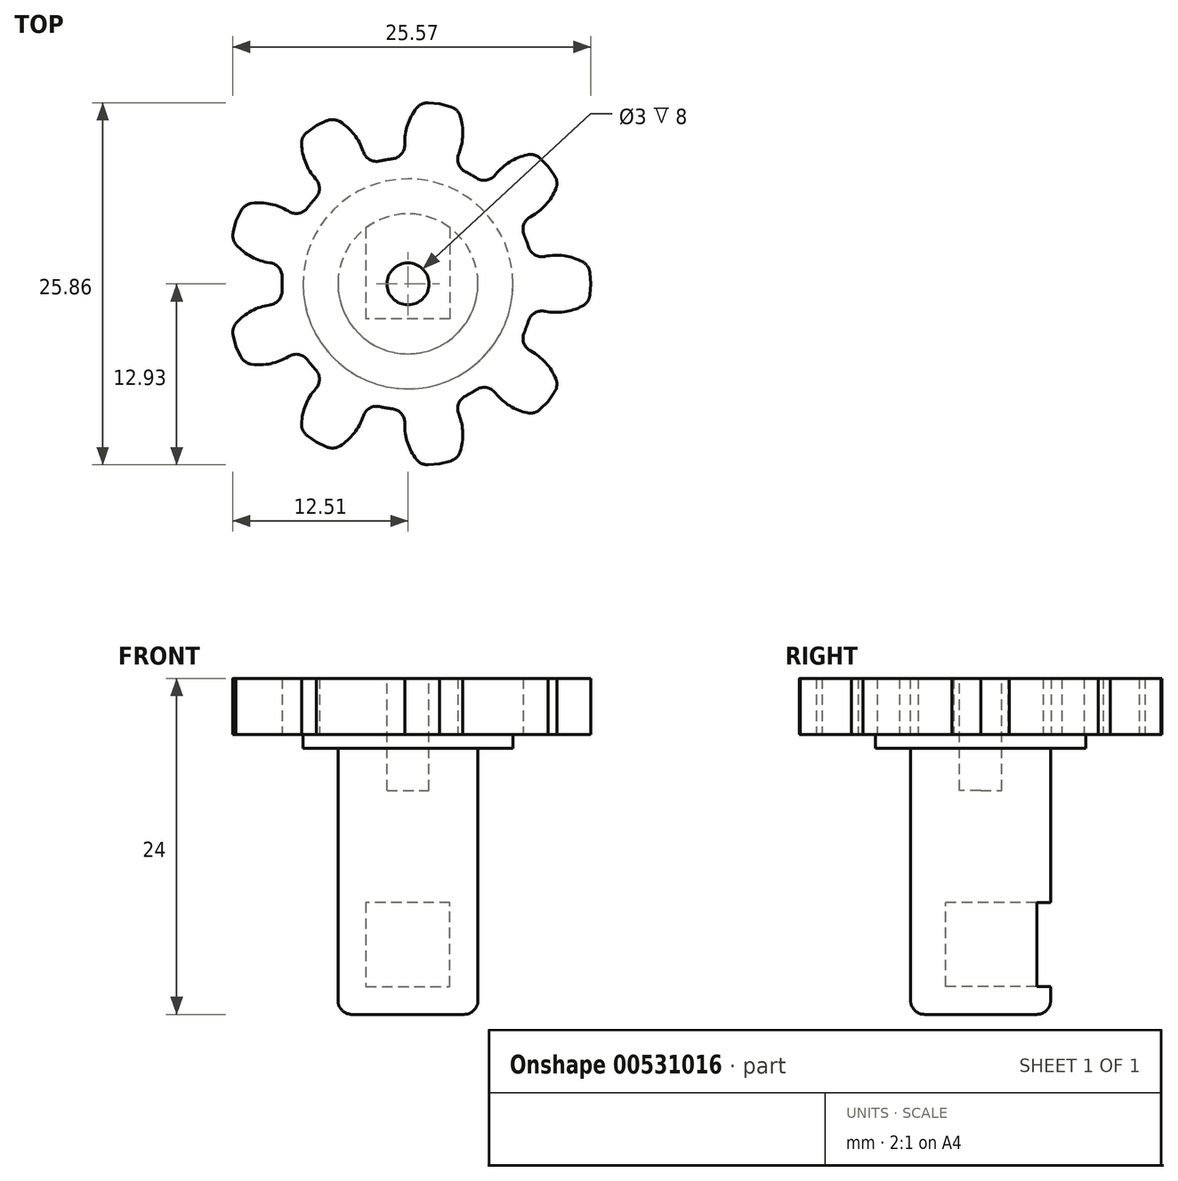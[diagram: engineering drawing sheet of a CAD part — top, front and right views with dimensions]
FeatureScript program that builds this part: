
annotation { "Feature Type Name" : "Feature", "Feature Type Description" : "" }
export const myFeature = defineFeature(function(context is Context, id is Id, definition is map)
    precondition{}
    {
        {
            var Q0;
            Q0=qCreatedBy(makeId("Top.planeOp"),FACE);
            var sketch = newSketch(context, id + "F0", { "sketchPlane" : qUnion([Q0])});
            skCircle(sketch, "E0", {"center": v(0, 0) * mm, "radius": 9 * mm, "construction": true});
            skLineSegment(sketch, "E1", {"start": v(0, 0) * mm, "end": v(11.56, 4.83) * mm, "construction": true});
            skLineSegment(sketch, "E2", {"start": v(0, 0) * mm, "end": v(13.06, 0) * mm, "construction": true});
            skLineSegment(sketch, "E3", {"start": v(0, 0) * mm, "end": v(8.3, 3.47) * mm});
            skLineSegment(sketch, "E4", {"start": v(0, 0) * mm, "end": v(9, 0) * mm});
            skLineSegment(sketch, "E5", {"start": v(0, 0) * mm, "end": v(9.8, 1.96) * mm, "construction": true});
            skLineSegment(sketch, "E6", {"start": v(0, 0) * mm, "end": v(12.94, 1.28) * mm, "construction": true});
            skArc(sketch, "E7", {"start": v(8.3, 3.47) * mm, "mid": v(8.46, 3.06) * mm, "end": v(8.6, 2.64) * mm});
            skLineSegment(sketch, "E8", {"start": v(9.76, 1.96) * mm, "end": v(9.8, 1.96) * mm});
            skLineSegment(sketch, "E9", {"start": v(12.98, 0.8) * mm, "end": v(13.06, 0) * mm});
            skLineSegment(sketch, "E10.MirrorCS", {"start": v(0, 0) * mm, "end": v(8.3, -3.47) * mm});
            skArc(sketch, "E11.MirrorCS", {"start": v(8.3, -3.47) * mm, "mid": v(8.46, -3.06) * mm, "end": v(8.6, -2.64) * mm});
            skLineSegment(sketch, "E12.MirrorCS", {"start": v(9.76, -1.96) * mm, "end": v(9.8, -1.96) * mm});
            skLineSegment(sketch, "E13.MirrorCS", {"start": v(12.98, -0.8) * mm, "end": v(13.06, 0) * mm});
            skPoint(sketch, "E14.visualSharp", {"position": v(8.82, 1.77) * mm});
            skArc(sketch, "E14.filletArc", {"start": v(8.6, 2.64) * mm, "mid": v(9.05, 2.08) * mm, "end": v(9.76, 1.96) * mm});
            skPoint(sketch, "E15.visualSharp", {"position": v(8.82, -1.77) * mm});
            skArc(sketch, "E15.filletArc", {"start": v(9.76, -1.96) * mm, "mid": v(9.05, -2.08) * mm, "end": v(8.6, -2.64) * mm});
            skPoint(sketch, "E16.visualSharp", {"position": v(12.94, -1.28) * mm});
            skArc(sketch, "E16.filletArc", {"start": v(12.46, -1.58) * mm, "mid": v(12.82, -1.26) * mm, "end": v(12.98, -0.8) * mm});
            skPoint(sketch, "E17.visualSharp", {"position": v(12.94, 1.28) * mm});
            skArc(sketch, "E17.filletArc", {"start": v(12.98, 0.8) * mm, "mid": v(12.82, 1.26) * mm, "end": v(12.46, 1.58) * mm});
            skArc(sketch, "E18", {"start": v(12.46, 1.58) * mm, "mid": v(11.16, 2) * mm, "end": v(9.8, 1.96) * mm});
            skArc(sketch, "E19", {"start": v(9.8, -1.96) * mm, "mid": v(11.16, -2) * mm, "end": v(12.46, -1.58) * mm});
            skSolve(sketch);
        }
        {
            var Q0;
            Q0=makeQuery(id+"F0.imprint","IMPRINT",FACE,{"disambiguationData":[TD([[makeQuery(id+"F0.imprint","IMPRINT",EDGE,{"derivedFrom":sQuery(id+"F0.wireOp",EDGE,"E3")}),-1.0]])]});
            extrude(context, id + "F1", {"entities" : qUnion([Q0]), "depth" : 4 * mm, "offsetDistance" : 25 * mm});
        }
        {
            var Q0;
            Q0=makeQuery(id+"F1.opExtrude","SWEPT_BODY",BODY,{"disambiguationData":[OSD([sQuery(id+"F0.wireOp",EDGE,"E3"),sQuery(id+"F0.wireOp",EDGE,"E7"),sQuery(id+"F0.wireOp",EDGE,"E8"),sQuery(id+"F0.wireOp",EDGE,"2mDmJFzi-9lNi-O13z-yd6C-LpkLtRZ1Arxh"),sQuery(id+"F0.wireOp",EDGE,"E9"),sQuery(id+"F0.wireOp",EDGE,"E10.MirrorCS"),sQuery(id+"F0.wireOp",EDGE,"E11.MirrorCS"),sQuery(id+"F0.wireOp",EDGE,"E12.MirrorCS"),sQuery(id+"F0.wireOp",EDGE,"b2a42f57-c3ba-47de-accf-343e7495cc910.MirrorCS"),sQuery(id+"F0.wireOp",EDGE,"E13.MirrorCS"),sQuery(id+"F0.wireOp",EDGE,"E14.filletArc"),sQuery(id+"F0.wireOp",EDGE,"E15.filletArc"),sQuery(id+"F0.wireOp",EDGE,"E16.filletArc"),sQuery(id+"F0.wireOp",EDGE,"E17.filletArc")])]});
            var Q1;
            Q1=makeQuery(id+"F1.opExtrude","SWEPT_EDGE",EDGE,{"disambiguationData":[OSD([sQuery(id+"F0.wireOp",EDGE,"E3"),sQuery(id+"F0.wireOp",EDGE,"E10.MirrorCS")])]});
            circularPattern(context, id + "F2", {"entities" : qUnion([Q0]), "axis" : qUnion([Q1]), "angle" : 360 * degree, "instanceCount" : 9, "equalSpace" : true, "computeTransformsWithoutBuiltin" : true});
        }
        {
            var Q0;
            Q0=makeQuery(id+"F2.opPattern","COPY",BODY,{"derivedFrom":makeQuery(id+"F1.opExtrude","SWEPT_BODY",BODY,{"disambiguationData":[OSD([sQuery(id+"F0.wireOp",EDGE,"E3"),sQuery(id+"F0.wireOp",EDGE,"E7"),sQuery(id+"F0.wireOp",EDGE,"E8"),sQuery(id+"F0.wireOp",EDGE,"2mDmJFzi-9lNi-O13z-yd6C-LpkLtRZ1Arxh"),sQuery(id+"F0.wireOp",EDGE,"E9"),sQuery(id+"F0.wireOp",EDGE,"E10.MirrorCS"),sQuery(id+"F0.wireOp",EDGE,"E11.MirrorCS"),sQuery(id+"F0.wireOp",EDGE,"E12.MirrorCS"),sQuery(id+"F0.wireOp",EDGE,"b2a42f57-c3ba-47de-accf-343e7495cc910.MirrorCS"),sQuery(id+"F0.wireOp",EDGE,"E13.MirrorCS"),sQuery(id+"F0.wireOp",EDGE,"E14.filletArc"),sQuery(id+"F0.wireOp",EDGE,"E15.filletArc"),sQuery(id+"F0.wireOp",EDGE,"E16.filletArc"),sQuery(id+"F0.wireOp",EDGE,"E17.filletArc")])]}),"instanceName":"7"});
            var Q1;
            Q1=makeQuery(id+"F2.opPattern","COPY",BODY,{"derivedFrom":makeQuery(id+"F1.opExtrude","SWEPT_BODY",BODY,{"disambiguationData":[OSD([sQuery(id+"F0.wireOp",EDGE,"E3"),sQuery(id+"F0.wireOp",EDGE,"E7"),sQuery(id+"F0.wireOp",EDGE,"E8"),sQuery(id+"F0.wireOp",EDGE,"2mDmJFzi-9lNi-O13z-yd6C-LpkLtRZ1Arxh"),sQuery(id+"F0.wireOp",EDGE,"E9"),sQuery(id+"F0.wireOp",EDGE,"E10.MirrorCS"),sQuery(id+"F0.wireOp",EDGE,"E11.MirrorCS"),sQuery(id+"F0.wireOp",EDGE,"E12.MirrorCS"),sQuery(id+"F0.wireOp",EDGE,"b2a42f57-c3ba-47de-accf-343e7495cc910.MirrorCS"),sQuery(id+"F0.wireOp",EDGE,"E13.MirrorCS"),sQuery(id+"F0.wireOp",EDGE,"E14.filletArc"),sQuery(id+"F0.wireOp",EDGE,"E15.filletArc"),sQuery(id+"F0.wireOp",EDGE,"E16.filletArc"),sQuery(id+"F0.wireOp",EDGE,"E17.filletArc")])]}),"instanceName":"6"});
            var Q2;
            Q2=makeQuery(id+"F2.opPattern","COPY",BODY,{"derivedFrom":makeQuery(id+"F1.opExtrude","SWEPT_BODY",BODY,{"disambiguationData":[OSD([sQuery(id+"F0.wireOp",EDGE,"E3"),sQuery(id+"F0.wireOp",EDGE,"E7"),sQuery(id+"F0.wireOp",EDGE,"E8"),sQuery(id+"F0.wireOp",EDGE,"2mDmJFzi-9lNi-O13z-yd6C-LpkLtRZ1Arxh"),sQuery(id+"F0.wireOp",EDGE,"E9"),sQuery(id+"F0.wireOp",EDGE,"E10.MirrorCS"),sQuery(id+"F0.wireOp",EDGE,"E11.MirrorCS"),sQuery(id+"F0.wireOp",EDGE,"E12.MirrorCS"),sQuery(id+"F0.wireOp",EDGE,"b2a42f57-c3ba-47de-accf-343e7495cc910.MirrorCS"),sQuery(id+"F0.wireOp",EDGE,"E13.MirrorCS"),sQuery(id+"F0.wireOp",EDGE,"E14.filletArc"),sQuery(id+"F0.wireOp",EDGE,"E15.filletArc"),sQuery(id+"F0.wireOp",EDGE,"E16.filletArc"),sQuery(id+"F0.wireOp",EDGE,"E17.filletArc")])]}),"instanceName":"4"});
            var Q3;
            Q3=makeQuery(id+"F2.opPattern","COPY",BODY,{"derivedFrom":makeQuery(id+"F1.opExtrude","SWEPT_BODY",BODY,{"disambiguationData":[OSD([sQuery(id+"F0.wireOp",EDGE,"E3"),sQuery(id+"F0.wireOp",EDGE,"E7"),sQuery(id+"F0.wireOp",EDGE,"E8"),sQuery(id+"F0.wireOp",EDGE,"2mDmJFzi-9lNi-O13z-yd6C-LpkLtRZ1Arxh"),sQuery(id+"F0.wireOp",EDGE,"E9"),sQuery(id+"F0.wireOp",EDGE,"E10.MirrorCS"),sQuery(id+"F0.wireOp",EDGE,"E11.MirrorCS"),sQuery(id+"F0.wireOp",EDGE,"E12.MirrorCS"),sQuery(id+"F0.wireOp",EDGE,"b2a42f57-c3ba-47de-accf-343e7495cc910.MirrorCS"),sQuery(id+"F0.wireOp",EDGE,"E13.MirrorCS"),sQuery(id+"F0.wireOp",EDGE,"E14.filletArc"),sQuery(id+"F0.wireOp",EDGE,"E15.filletArc"),sQuery(id+"F0.wireOp",EDGE,"E16.filletArc"),sQuery(id+"F0.wireOp",EDGE,"E17.filletArc")])]}),"instanceName":"5"});
            var Q4;
            Q4=makeQuery(id+"F1.opExtrude","SWEPT_BODY",BODY,{"disambiguationData":[OSD([sQuery(id+"F0.wireOp",EDGE,"E3"),sQuery(id+"F0.wireOp",EDGE,"E7"),sQuery(id+"F0.wireOp",EDGE,"E8"),sQuery(id+"F0.wireOp",EDGE,"2mDmJFzi-9lNi-O13z-yd6C-LpkLtRZ1Arxh"),sQuery(id+"F0.wireOp",EDGE,"E9"),sQuery(id+"F0.wireOp",EDGE,"E10.MirrorCS"),sQuery(id+"F0.wireOp",EDGE,"E11.MirrorCS"),sQuery(id+"F0.wireOp",EDGE,"E12.MirrorCS"),sQuery(id+"F0.wireOp",EDGE,"b2a42f57-c3ba-47de-accf-343e7495cc910.MirrorCS"),sQuery(id+"F0.wireOp",EDGE,"E13.MirrorCS"),sQuery(id+"F0.wireOp",EDGE,"E14.filletArc"),sQuery(id+"F0.wireOp",EDGE,"E15.filletArc"),sQuery(id+"F0.wireOp",EDGE,"E16.filletArc"),sQuery(id+"F0.wireOp",EDGE,"E17.filletArc")])]});
            var Q5;
            Q5=makeQuery(id+"F2.opPattern","COPY",BODY,{"derivedFrom":makeQuery(id+"F1.opExtrude","SWEPT_BODY",BODY,{"disambiguationData":[OSD([sQuery(id+"F0.wireOp",EDGE,"E3"),sQuery(id+"F0.wireOp",EDGE,"E7"),sQuery(id+"F0.wireOp",EDGE,"E8"),sQuery(id+"F0.wireOp",EDGE,"2mDmJFzi-9lNi-O13z-yd6C-LpkLtRZ1Arxh"),sQuery(id+"F0.wireOp",EDGE,"E9"),sQuery(id+"F0.wireOp",EDGE,"E10.MirrorCS"),sQuery(id+"F0.wireOp",EDGE,"E11.MirrorCS"),sQuery(id+"F0.wireOp",EDGE,"E12.MirrorCS"),sQuery(id+"F0.wireOp",EDGE,"b2a42f57-c3ba-47de-accf-343e7495cc910.MirrorCS"),sQuery(id+"F0.wireOp",EDGE,"E13.MirrorCS"),sQuery(id+"F0.wireOp",EDGE,"E14.filletArc"),sQuery(id+"F0.wireOp",EDGE,"E15.filletArc"),sQuery(id+"F0.wireOp",EDGE,"E16.filletArc"),sQuery(id+"F0.wireOp",EDGE,"E17.filletArc")])]}),"instanceName":"1"});
            var Q6;
            Q6=makeQuery(id+"F2.opPattern","COPY",BODY,{"derivedFrom":makeQuery(id+"F1.opExtrude","SWEPT_BODY",BODY,{"disambiguationData":[OSD([sQuery(id+"F0.wireOp",EDGE,"E3"),sQuery(id+"F0.wireOp",EDGE,"E7"),sQuery(id+"F0.wireOp",EDGE,"E8"),sQuery(id+"F0.wireOp",EDGE,"2mDmJFzi-9lNi-O13z-yd6C-LpkLtRZ1Arxh"),sQuery(id+"F0.wireOp",EDGE,"E9"),sQuery(id+"F0.wireOp",EDGE,"E10.MirrorCS"),sQuery(id+"F0.wireOp",EDGE,"E11.MirrorCS"),sQuery(id+"F0.wireOp",EDGE,"E12.MirrorCS"),sQuery(id+"F0.wireOp",EDGE,"b2a42f57-c3ba-47de-accf-343e7495cc910.MirrorCS"),sQuery(id+"F0.wireOp",EDGE,"E13.MirrorCS"),sQuery(id+"F0.wireOp",EDGE,"E14.filletArc"),sQuery(id+"F0.wireOp",EDGE,"E15.filletArc"),sQuery(id+"F0.wireOp",EDGE,"E16.filletArc"),sQuery(id+"F0.wireOp",EDGE,"E17.filletArc")])]}),"instanceName":"3"});
            var Q7;
            Q7=makeQuery(id+"F2.opPattern","COPY",BODY,{"derivedFrom":makeQuery(id+"F1.opExtrude","SWEPT_BODY",BODY,{"disambiguationData":[OSD([sQuery(id+"F0.wireOp",EDGE,"E3"),sQuery(id+"F0.wireOp",EDGE,"E7"),sQuery(id+"F0.wireOp",EDGE,"E8"),sQuery(id+"F0.wireOp",EDGE,"2mDmJFzi-9lNi-O13z-yd6C-LpkLtRZ1Arxh"),sQuery(id+"F0.wireOp",EDGE,"E9"),sQuery(id+"F0.wireOp",EDGE,"E10.MirrorCS"),sQuery(id+"F0.wireOp",EDGE,"E11.MirrorCS"),sQuery(id+"F0.wireOp",EDGE,"E12.MirrorCS"),sQuery(id+"F0.wireOp",EDGE,"b2a42f57-c3ba-47de-accf-343e7495cc910.MirrorCS"),sQuery(id+"F0.wireOp",EDGE,"E13.MirrorCS"),sQuery(id+"F0.wireOp",EDGE,"E14.filletArc"),sQuery(id+"F0.wireOp",EDGE,"E15.filletArc"),sQuery(id+"F0.wireOp",EDGE,"E16.filletArc"),sQuery(id+"F0.wireOp",EDGE,"E17.filletArc")])]}),"instanceName":"2"});
            var Q8;
            Q8=makeQuery(id+"F2.opPattern","COPY",BODY,{"derivedFrom":makeQuery(id+"F1.opExtrude","SWEPT_BODY",BODY,{"disambiguationData":[OSD([sQuery(id+"F0.wireOp",EDGE,"E3"),sQuery(id+"F0.wireOp",EDGE,"E7"),sQuery(id+"F0.wireOp",EDGE,"E8"),sQuery(id+"F0.wireOp",EDGE,"E9"),sQuery(id+"F0.wireOp",EDGE,"E10.MirrorCS"),sQuery(id+"F0.wireOp",EDGE,"E11.MirrorCS"),sQuery(id+"F0.wireOp",EDGE,"E12.MirrorCS"),sQuery(id+"F0.wireOp",EDGE,"E13.MirrorCS"),sQuery(id+"F0.wireOp",EDGE,"E14.filletArc"),sQuery(id+"F0.wireOp",EDGE,"E15.filletArc"),sQuery(id+"F0.wireOp",EDGE,"E16.filletArc"),sQuery(id+"F0.wireOp",EDGE,"E17.filletArc"),sQuery(id+"F0.wireOp",EDGE,"E18"),sQuery(id+"F0.wireOp",EDGE,"E19")])]}),"instanceName":"8"});
            booleanBodies(context, id + "F3", {"operationType" : BooleanOperationType.UNION, "tools" : qUnion([Q0, Q1, Q2, Q3, Q4, Q5, Q6, Q7, Q8])});
        }
        {
            var Q0;
            {var subQ0=makeQuery(id+"F1.opExtrude","CAP_FACE",FACE,{"disambiguationData":[OSD([sQuery(id+"F0.wireOp",EDGE,"E3"),sQuery(id+"F0.wireOp",EDGE,"E7"),sQuery(id+"F0.wireOp",EDGE,"E8"),sQuery(id+"F0.wireOp",EDGE,"E9"),sQuery(id+"F0.wireOp",EDGE,"E10.MirrorCS"),sQuery(id+"F0.wireOp",EDGE,"E11.MirrorCS"),sQuery(id+"F0.wireOp",EDGE,"E12.MirrorCS"),sQuery(id+"F0.wireOp",EDGE,"E13.MirrorCS"),sQuery(id+"F0.wireOp",EDGE,"E14.filletArc"),sQuery(id+"F0.wireOp",EDGE,"E15.filletArc"),sQuery(id+"F0.wireOp",EDGE,"E16.filletArc"),sQuery(id+"F0.wireOp",EDGE,"E17.filletArc"),sQuery(id+"F0.wireOp",EDGE,"E18"),sQuery(id+"F0.wireOp",EDGE,"E19")])],"isStart":false});Q0=makeQuery(id+"F3.opBoolean","MERGE",FACE,{"derivedFrom":[subQ0,makeQuery(id+"F2.opPattern","COPY",FACE,{"derivedFrom":subQ0,"instanceName":"1"}),makeQuery(id+"F2.opPattern","COPY",FACE,{"derivedFrom":subQ0,"instanceName":"2"}),makeQuery(id+"F2.opPattern","COPY",FACE,{"derivedFrom":subQ0,"instanceName":"3"}),makeQuery(id+"F2.opPattern","COPY",FACE,{"derivedFrom":subQ0,"instanceName":"4"}),makeQuery(id+"F2.opPattern","COPY",FACE,{"derivedFrom":subQ0,"instanceName":"5"}),makeQuery(id+"F2.opPattern","COPY",FACE,{"derivedFrom":subQ0,"instanceName":"6"}),makeQuery(id+"F2.opPattern","COPY",FACE,{"derivedFrom":subQ0,"instanceName":"7"}),makeQuery(id+"F2.opPattern","COPY",FACE,{"derivedFrom":subQ0,"instanceName":"8"})]});}
            var sketch = newSketch(context, id + "F4", { "sketchPlane" : qUnion([Q0])});
            skCircle(sketch, "E20", {"center": v(0, 0) * mm, "radius": 1.5 * mm});
            skSolve(sketch);
        }
        {
            var Q0;
            Q0 = qSketchRegion(id + "F4", true);
            var Q1;
            {var subQ0=makeQuery(id+"F1.opExtrude","CAP_FACE",FACE,{"disambiguationData":[OSD([sQuery(id+"F0.wireOp",EDGE,"E3"),sQuery(id+"F0.wireOp",EDGE,"E7"),sQuery(id+"F0.wireOp",EDGE,"E8"),sQuery(id+"F0.wireOp",EDGE,"E9"),sQuery(id+"F0.wireOp",EDGE,"E10.MirrorCS"),sQuery(id+"F0.wireOp",EDGE,"E11.MirrorCS"),sQuery(id+"F0.wireOp",EDGE,"E12.MirrorCS"),sQuery(id+"F0.wireOp",EDGE,"E13.MirrorCS"),sQuery(id+"F0.wireOp",EDGE,"E14.filletArc"),sQuery(id+"F0.wireOp",EDGE,"E15.filletArc"),sQuery(id+"F0.wireOp",EDGE,"E16.filletArc"),sQuery(id+"F0.wireOp",EDGE,"E17.filletArc"),sQuery(id+"F0.wireOp",EDGE,"E18"),sQuery(id+"F0.wireOp",EDGE,"E19")])],"isStart":true});Q1=makeQuery(id+"F3.opBoolean","MERGE",FACE,{"derivedFrom":[subQ0,makeQuery(id+"F2.opPattern","COPY",FACE,{"derivedFrom":subQ0,"instanceName":"1"}),makeQuery(id+"F2.opPattern","COPY",FACE,{"derivedFrom":subQ0,"instanceName":"2"}),makeQuery(id+"F2.opPattern","COPY",FACE,{"derivedFrom":subQ0,"instanceName":"3"}),makeQuery(id+"F2.opPattern","COPY",FACE,{"derivedFrom":subQ0,"instanceName":"4"}),makeQuery(id+"F2.opPattern","COPY",FACE,{"derivedFrom":subQ0,"instanceName":"5"}),makeQuery(id+"F2.opPattern","COPY",FACE,{"derivedFrom":subQ0,"instanceName":"6"}),makeQuery(id+"F2.opPattern","COPY",FACE,{"derivedFrom":subQ0,"instanceName":"7"}),makeQuery(id+"F2.opPattern","COPY",FACE,{"derivedFrom":subQ0,"instanceName":"8"})]});}
            extrude(context, id + "F5", {"entities" : qUnion([Q0]), "operationType" : NewBodyOperationType.REMOVE, "endBound" : BoundingType.UP_TO_SURFACE, "oppositeDirection" : true, "depth" : 25 * mm, "endBoundEntityFace" : qUnion([Q1]), "offsetDistance" : 25 * mm});
        }
        {
            var Q0;
            {var subQ0=makeQuery(id+"F1.opExtrude","CAP_FACE",FACE,{"disambiguationData":[OSD([sQuery(id+"F0.wireOp",EDGE,"E3"),sQuery(id+"F0.wireOp",EDGE,"E7"),sQuery(id+"F0.wireOp",EDGE,"E8"),sQuery(id+"F0.wireOp",EDGE,"E9"),sQuery(id+"F0.wireOp",EDGE,"E10.MirrorCS"),sQuery(id+"F0.wireOp",EDGE,"E11.MirrorCS"),sQuery(id+"F0.wireOp",EDGE,"E12.MirrorCS"),sQuery(id+"F0.wireOp",EDGE,"E13.MirrorCS"),sQuery(id+"F0.wireOp",EDGE,"E14.filletArc"),sQuery(id+"F0.wireOp",EDGE,"E15.filletArc"),sQuery(id+"F0.wireOp",EDGE,"E16.filletArc"),sQuery(id+"F0.wireOp",EDGE,"E17.filletArc"),sQuery(id+"F0.wireOp",EDGE,"E18"),sQuery(id+"F0.wireOp",EDGE,"E19")])],"isStart":true});Q0=makeQuery(id+"F3.opBoolean","MERGE",FACE,{"derivedFrom":[subQ0,makeQuery(id+"F2.opPattern","COPY",FACE,{"derivedFrom":subQ0,"instanceName":"1"}),makeQuery(id+"F2.opPattern","COPY",FACE,{"derivedFrom":subQ0,"instanceName":"2"}),makeQuery(id+"F2.opPattern","COPY",FACE,{"derivedFrom":subQ0,"instanceName":"3"}),makeQuery(id+"F2.opPattern","COPY",FACE,{"derivedFrom":subQ0,"instanceName":"4"}),makeQuery(id+"F2.opPattern","COPY",FACE,{"derivedFrom":subQ0,"instanceName":"5"}),makeQuery(id+"F2.opPattern","COPY",FACE,{"derivedFrom":subQ0,"instanceName":"6"}),makeQuery(id+"F2.opPattern","COPY",FACE,{"derivedFrom":subQ0,"instanceName":"7"}),makeQuery(id+"F2.opPattern","COPY",FACE,{"derivedFrom":subQ0,"instanceName":"8"})]});}
            var sketch = newSketch(context, id + "F6", { "sketchPlane" : qUnion([Q0])});
            skCircle(sketch, "E21", {"center": v(0, 0) * mm, "radius": 5 * mm});
            skSolve(sketch);
        }
        {
            var Q0;
            Q0 = qSketchRegion(id + "F6", true);
            extrude(context, id + "F7", {"entities" : qUnion([Q0]), "operationType" : NewBodyOperationType.ADD, "depth" : 20 * mm, "offsetDistance" : 25 * mm});
        }
        {
            var Q0;
            Q0=makeQuery(id+"F7.opExtrude","CAP_FACE",FACE,{"disambiguationData":[OSD([sQuery(id+"F6.wireOp",EDGE,"E21")])],"isStart":true});
            extrude(context, id + "F8", {"entities" : qUnion([Q0]), "operationType" : NewBodyOperationType.REMOVE, "oppositeDirection" : true, "depth" : 4 * mm, "offsetDistance" : 25 * mm});
        }
        {
            var Q0;
            Q0=qCreatedBy(makeId("Front.planeOp"),FACE);
            var sketch = newSketch(context, id + "F9", { "sketchPlane" : qUnion([Q0])});
            skLineSegment(sketch, "E22", {"start": v(0, 0) * mm, "end": v(0, -12) * mm, "construction": true});
            skLineSegment(sketch, "E23", {"start": v(0, -12) * mm, "end": v(-3, -12) * mm});
            skLineSegment(sketch, "E24", {"start": v(-3, -12) * mm, "end": v(-3, -18) * mm});
            skLineSegment(sketch, "E25", {"start": v(-3, -18) * mm, "end": v(3, -18) * mm});
            skLineSegment(sketch, "E26", {"start": v(3, -18) * mm, "end": v(3, -12) * mm});
            skLineSegment(sketch, "E27", {"start": v(3, -12) * mm, "end": v(0, -12) * mm});
            skSolve(sketch);
        }
        {
            var Q0;
            Q0 = qSketchRegion(id + "F9", true);
            var Q1;
            Q1=makeQuery(id+"F7.opExtrude","SWEPT_FACE",FACE,{"disambiguationData":[OSD([sQuery(id+"F6.wireOp",EDGE,"E21")])]});
            extrude(context, id + "F10", {"entities" : qUnion([Q0]), "operationType" : NewBodyOperationType.REMOVE, "endBound" : BoundingType.UP_TO_SURFACE, "oppositeDirection" : true, "depth" : 25 * mm, "endBoundEntityFace" : qUnion([Q1]), "offsetDistance" : 25 * mm});
        }
        {
            var Q0;
            Q0=makeQuery(id+"F10.boolean.opBoolean","COPY",FACE,{"derivedFrom":makeQuery(id+"F10.opExtrude","CAP_FACE",FACE,{"disambiguationData":[OSD([sQuery(id+"F9.wireOp",EDGE,"E23"),sQuery(id+"F9.wireOp",EDGE,"E24"),sQuery(id+"F9.wireOp",EDGE,"E25"),sQuery(id+"F9.wireOp",EDGE,"E26"),sQuery(id+"F9.wireOp",EDGE,"E27")])],"isStart":true})});
            extrude(context, id + "F11", {"entities" : qUnion([Q0]), "operationType" : NewBodyOperationType.REMOVE, "oppositeDirection" : true, "depth" : 2.5 * mm, "offsetDistance" : 25 * mm});
        }
        {
            var Q0;
            Q0=makeQuery(id+"F7.opExtrude","CAP_EDGE",EDGE,{"disambiguationData":[OSD([sQuery(id+"F6.wireOp",EDGE,"E21")])],"isStart":false});
            fillet(context, id + "F12", {"entities" : qUnion([Q0]), "radius" : 1 * mm, "tangentPropagation" : true, "allowEdgeOverflow" : false});
        }
        {
            var Q0;
            {var subQ0=makeQuery(id+"F1.opExtrude","CAP_FACE",FACE,{"disambiguationData":[OSD([sQuery(id+"F0.wireOp",EDGE,"E3"),sQuery(id+"F0.wireOp",EDGE,"E7"),sQuery(id+"F0.wireOp",EDGE,"E8"),sQuery(id+"F0.wireOp",EDGE,"E9"),sQuery(id+"F0.wireOp",EDGE,"E10.MirrorCS"),sQuery(id+"F0.wireOp",EDGE,"E11.MirrorCS"),sQuery(id+"F0.wireOp",EDGE,"E12.MirrorCS"),sQuery(id+"F0.wireOp",EDGE,"E13.MirrorCS"),sQuery(id+"F0.wireOp",EDGE,"E14.filletArc"),sQuery(id+"F0.wireOp",EDGE,"E15.filletArc"),sQuery(id+"F0.wireOp",EDGE,"E16.filletArc"),sQuery(id+"F0.wireOp",EDGE,"E17.filletArc"),sQuery(id+"F0.wireOp",EDGE,"E18"),sQuery(id+"F0.wireOp",EDGE,"E19")])],"isStart":true});Q0=makeQuery(id+"F3.opBoolean","MERGE",FACE,{"derivedFrom":[subQ0,makeQuery(id+"F2.opPattern","COPY",FACE,{"derivedFrom":subQ0,"instanceName":"1"}),makeQuery(id+"F2.opPattern","COPY",FACE,{"derivedFrom":subQ0,"instanceName":"2"}),makeQuery(id+"F2.opPattern","COPY",FACE,{"derivedFrom":subQ0,"instanceName":"3"}),makeQuery(id+"F2.opPattern","COPY",FACE,{"derivedFrom":subQ0,"instanceName":"4"}),makeQuery(id+"F2.opPattern","COPY",FACE,{"derivedFrom":subQ0,"instanceName":"5"}),makeQuery(id+"F2.opPattern","COPY",FACE,{"derivedFrom":subQ0,"instanceName":"6"}),makeQuery(id+"F2.opPattern","COPY",FACE,{"derivedFrom":subQ0,"instanceName":"7"}),makeQuery(id+"F2.opPattern","COPY",FACE,{"derivedFrom":subQ0,"instanceName":"8"})]});}
            var sketch = newSketch(context, id + "F13", { "sketchPlane" : qUnion([Q0])});
            skCircle(sketch, "E28", {"center": v(0, 0) * mm, "radius": 7.5 * mm});
            skSolve(sketch);
        }
        {
            var Q0;
            Q0=makeQuery(id+"F13.imprint","IMPRINT",FACE,{"disambiguationData":[TD([[makeQuery(id+"F13.imprint","IMPRINT",EDGE,{"derivedFrom":sQuery(id+"F13.wireOp",EDGE,"E28")}),1.0]])]});
            extrude(context, id + "F14", {"entities" : qUnion([Q0]), "operationType" : NewBodyOperationType.ADD, "depth" : 1 * mm, "offsetDistance" : 25 * mm});
        }
    });
